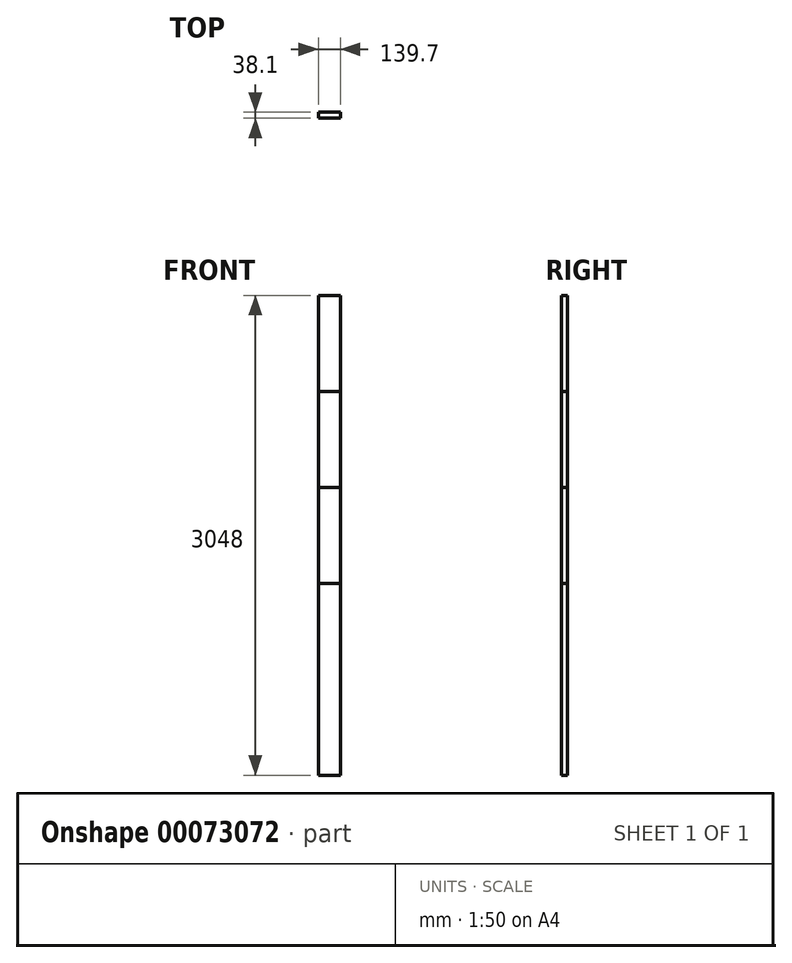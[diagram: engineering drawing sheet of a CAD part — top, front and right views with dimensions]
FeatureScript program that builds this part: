
annotation { "Feature Type Name" : "Feature", "Feature Type Description" : "" }
export const myFeature = defineFeature(function(context is Context, id is Id, definition is map)
    precondition{}
    {
        {
            var Q0;
            Q0=qCreatedBy(makeId("Top.planeOp"),FACE);
            var sketch = newSketch(context, id + "F0", { "sketchPlane" : qUnion([Q0])});
            skLineSegment(sketch, "E0.rect.bottom", {"start": v(69.85, -19.05) * mm, "end": v(-69.85, -19.05) * mm});
            skLineSegment(sketch, "E0.rect.top", {"start": v(69.85, 19.05) * mm, "end": v(-69.85, 19.05) * mm});
            skLineSegment(sketch, "E0.rect.left", {"start": v(69.85, -19.05) * mm, "end": v(69.85, 19.05) * mm});
            skLineSegment(sketch, "E0.rect.right", {"start": v(-69.85, -19.05) * mm, "end": v(-69.85, 19.05) * mm});
            skPoint(sketch, "E0.rect.middle", {"position": v(0, 0) * mm});
            skSolve(sketch);
        }
        {
            var Q0;
            Q0 = qSketchRegion(id + "F0", true);
            extrude(context, id + "F1", {"entities" : qUnion([Q0]), "depth" : 3048 * mm});
        }
        {
            var Q0;
            Q0 = qSketchRegion(id + "F0", true);
            extrude(context, id + "F2", {"entities" : qUnion([Q0]), "depth" : 2438.4 * mm});
        }
        {
            var Q0;
            Q0 = qSketchRegion(id + "F0", true);
            extrude(context, id + "F3", {"entities" : qUnion([Q0]), "depth" : 1828.8 * mm});
        }
        {
            var Q0;
            Q0 = qSketchRegion(id + "F0", true);
            extrude(context, id + "F4", {"entities" : qUnion([Q0]), "depth" : 1219.2 * mm});
        }
    });
